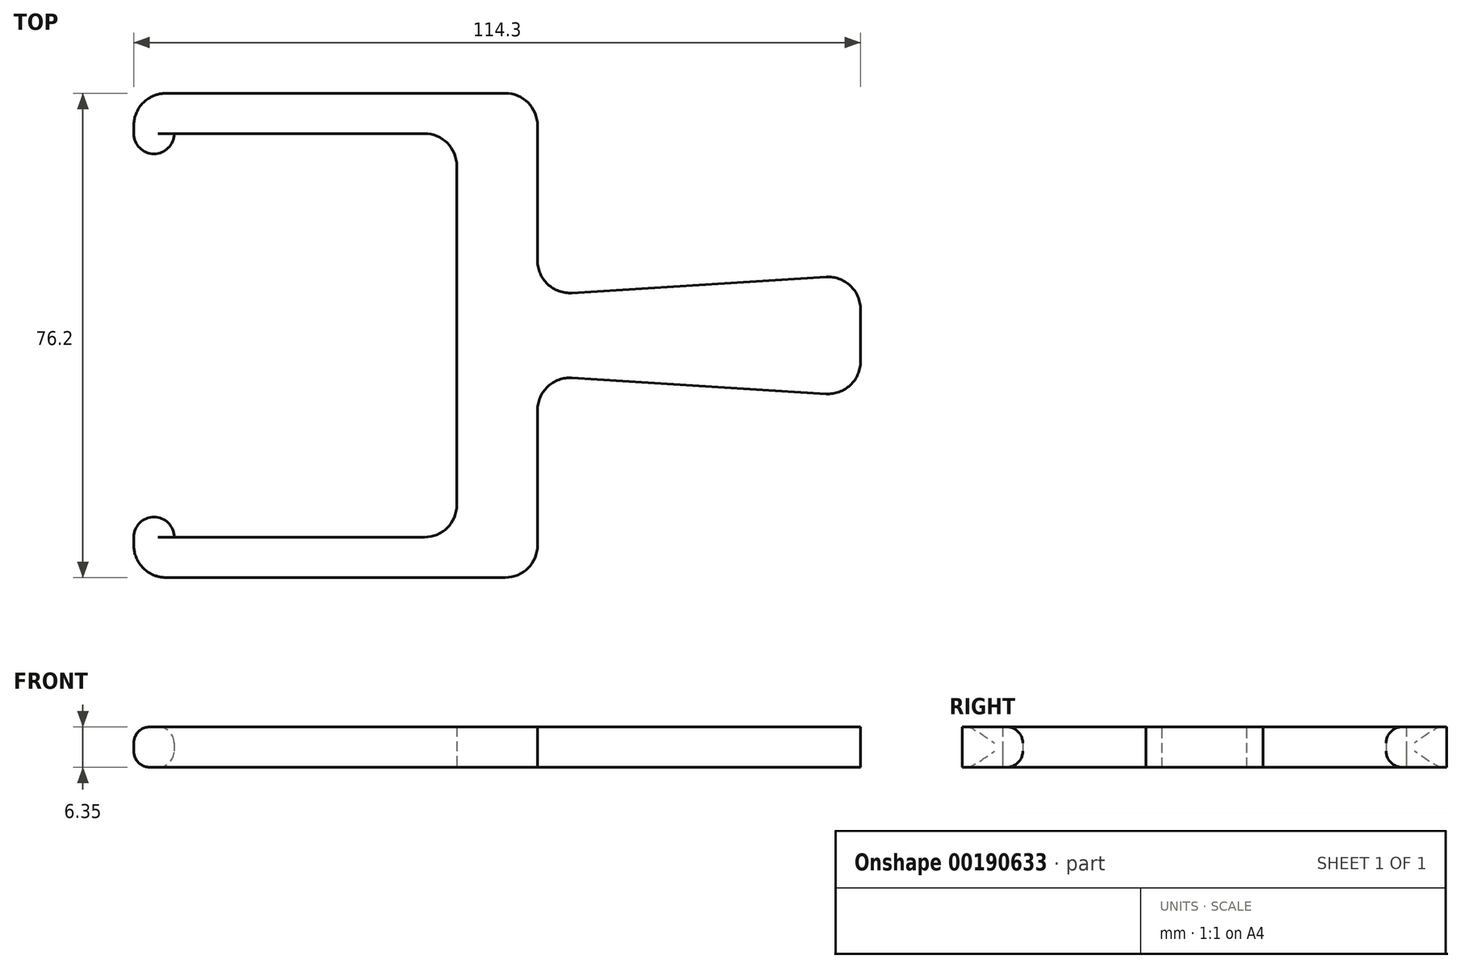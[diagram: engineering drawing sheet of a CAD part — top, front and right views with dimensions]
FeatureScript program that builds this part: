
annotation { "Feature Type Name" : "Feature", "Feature Type Description" : "" }
export const myFeature = defineFeature(function(context is Context, id is Id, definition is map)
    precondition{}
    {
        {
            var Q0;
            Q0=qCreatedBy(makeId("Top.planeOp"),FACE);
            var sketch = newSketch(context, id + "F0", { "sketchPlane" : qUnion([Q0])});
            skLineSegment(sketch, "E0.bottom", {"start": v(31.75, -38.1) * mm, "end": v(-31.75, -38.1) * mm});
            skLineSegment(sketch, "E0.top", {"start": v(31.75, 38.1) * mm, "end": v(-31.75, 38.1) * mm});
            skLineSegment(sketch, "E0.left", {"start": v(31.75, -38.1) * mm, "end": v(31.75, -6.35) * mm});
            skLineSegment(sketch, "E0.right", {"start": v(-31.75, -38.1) * mm, "end": v(-31.75, -31.75) * mm});
            skPoint(sketch, "E0.middle", {"position": v(0, 0) * mm});
            skLineSegment(sketch, "E1.top", {"start": v(-25.4, -31.75) * mm, "end": v(19.05, -31.75) * mm});
            skLineSegment(sketch, "E1.right", {"start": v(19.05, 31.75) * mm, "end": v(19.05, -31.75) * mm});
            skLineSegment(sketch, "E2.trimOffspring", {"start": v(-31.75, 31.75) * mm, "end": v(-31.75, 38.1) * mm});
            skArc(sketch, "E3", {"start": v(-31.75, 31.75) * mm, "mid": v(-28.58, 28.57) * mm, "end": v(-25.4, 31.75) * mm});
            skArc(sketch, "E4", {"start": v(-25.4, -31.75) * mm, "mid": v(-28.57, -28.58) * mm, "end": v(-31.75, -31.75) * mm});
            skLineSegment(sketch, "E5.trimOffspring", {"start": v(-25.4, 31.75) * mm, "end": v(19.05, 31.75) * mm});
            skLineSegment(sketch, "E6", {"start": v(31.75, -6.35) * mm, "end": v(82.55, -9.52) * mm});
            skLineSegment(sketch, "E7", {"start": v(82.55, -9.52) * mm, "end": v(82.55, 9.53) * mm});
            skLineSegment(sketch, "E8", {"start": v(82.55, 9.53) * mm, "end": v(31.75, 6.35) * mm});
            skLineSegment(sketch, "E9.trimOffspring", {"start": v(31.75, 6.35) * mm, "end": v(31.75, 38.1) * mm});
            skSolve(sketch);
        }
        {
            var Q0;
            Q0 = qSketchRegion(id + "F0", true);
            extrude(context, id + "F1", {"entities" : qUnion([Q0]), "depth" : 6.35 * mm});
        }
        {
            var Q0;
            Q0=makeQuery(id+"F1.opExtrude","SWEPT_EDGE",EDGE,{"disambiguationData":[OSD([sQuery(id+"F0.wireOp",EDGE,"E1.bottom"),sQuery(id+"F0.wireOp",EDGE,"E1.right")])]});
            var Q1;
            Q1=makeQuery(id+"F1.opExtrude","SWEPT_EDGE",EDGE,{"disambiguationData":[OSD([sQuery(id+"F0.wireOp",EDGE,"E1.top"),sQuery(id+"F0.wireOp",EDGE,"E1.right")])]});
            var Q2;
            Q2=makeQuery(id+"F1.opExtrude","SWEPT_EDGE",EDGE,{"disambiguationData":[OSD([sQuery(id+"F0.wireOp",EDGE,"E0.top"),sQuery(id+"F0.wireOp",EDGE,"E0.left")])]});
            var Q3;
            Q3=makeQuery(id+"F1.opExtrude","SWEPT_EDGE",EDGE,{"disambiguationData":[OSD([sQuery(id+"F0.wireOp",EDGE,"E0.bottom"),sQuery(id+"F0.wireOp",EDGE,"E0.left")])]});
            var Q4;
            Q4=makeQuery(id+"F1.opExtrude","SWEPT_EDGE",EDGE,{"disambiguationData":[OSD([sQuery(id+"F0.wireOp",EDGE,"E0.bottom"),sQuery(id+"F0.wireOp",EDGE,"E0.right")])]});
            var Q5;
            Q5=makeQuery(id+"F1.opExtrude","SWEPT_EDGE",EDGE,{"disambiguationData":[OSD([sQuery(id+"F0.wireOp",EDGE,"E8"),sQuery(id+"F0.wireOp",EDGE,"E9.trimOffspring")])]});
            var Q6;
            Q6=makeQuery(id+"F1.opExtrude","SWEPT_EDGE",EDGE,{"disambiguationData":[OSD([sQuery(id+"F0.wireOp",EDGE,"E6"),sQuery(id+"F0.wireOp",EDGE,"E7")])]});
            var Q7;
            Q7=makeQuery(id+"F1.opExtrude","SWEPT_EDGE",EDGE,{"disambiguationData":[OSD([sQuery(id+"F0.wireOp",EDGE,"E7"),sQuery(id+"F0.wireOp",EDGE,"E8")])]});
            fillet(context, id + "F2", {"entities" : qUnion([Q0, Q1, Q2, Q3, Q4, Q5, Q6, Q7]), "radius" : 5.08 * mm, "tangentPropagation" : true, "allowEdgeOverflow" : false});
        }
        {
            var Q0;
            Q0=makeQuery(id+"F1.opExtrude","CAP_EDGE",EDGE,{"disambiguationData":[OSD([sQuery(id+"F0.wireOp",EDGE,"E3")])],"isStart":false});
            var Q1;
            Q1=makeQuery(id+"F1.opExtrude","CAP_EDGE",EDGE,{"disambiguationData":[OSD([sQuery(id+"F0.wireOp",EDGE,"E2.trimOffspring")])],"isStart":false});
            var Q2;
            Q2=makeQuery(id+"F1.opExtrude","CAP_EDGE",EDGE,{"disambiguationData":[OSD([sQuery(id+"F0.wireOp",EDGE,"E2.trimOffspring")])],"isStart":true});
            var Q3;
            Q3=makeQuery(id+"F1.opExtrude","CAP_EDGE",EDGE,{"disambiguationData":[OSD([sQuery(id+"F0.wireOp",EDGE,"E3")])],"isStart":true});
            var Q4;
            Q4=makeQuery(id+"F1.opExtrude","CAP_EDGE",EDGE,{"disambiguationData":[OSD([sQuery(id+"F0.wireOp",EDGE,"E0.right")])],"isStart":false});
            var Q5;
            Q5=makeQuery(id+"F1.opExtrude","CAP_EDGE",EDGE,{"disambiguationData":[OSD([sQuery(id+"F0.wireOp",EDGE,"E4")])],"isStart":false});
            var Q6;
            Q6=makeQuery(id+"F1.opExtrude","CAP_EDGE",EDGE,{"disambiguationData":[OSD([sQuery(id+"F0.wireOp",EDGE,"E0.right")])],"isStart":true});
            var Q7;
            Q7=makeQuery(id+"F1.opExtrude","CAP_EDGE",EDGE,{"disambiguationData":[OSD([sQuery(id+"F0.wireOp",EDGE,"E4")])],"isStart":true});
            fillet(context, id + "F3", {"entities" : qUnion([Q0, Q1, Q2, Q3, Q4, Q5, Q6, Q7]), "radius" : 2.54 * mm, "allowEdgeOverflow" : false});
        }
    });
